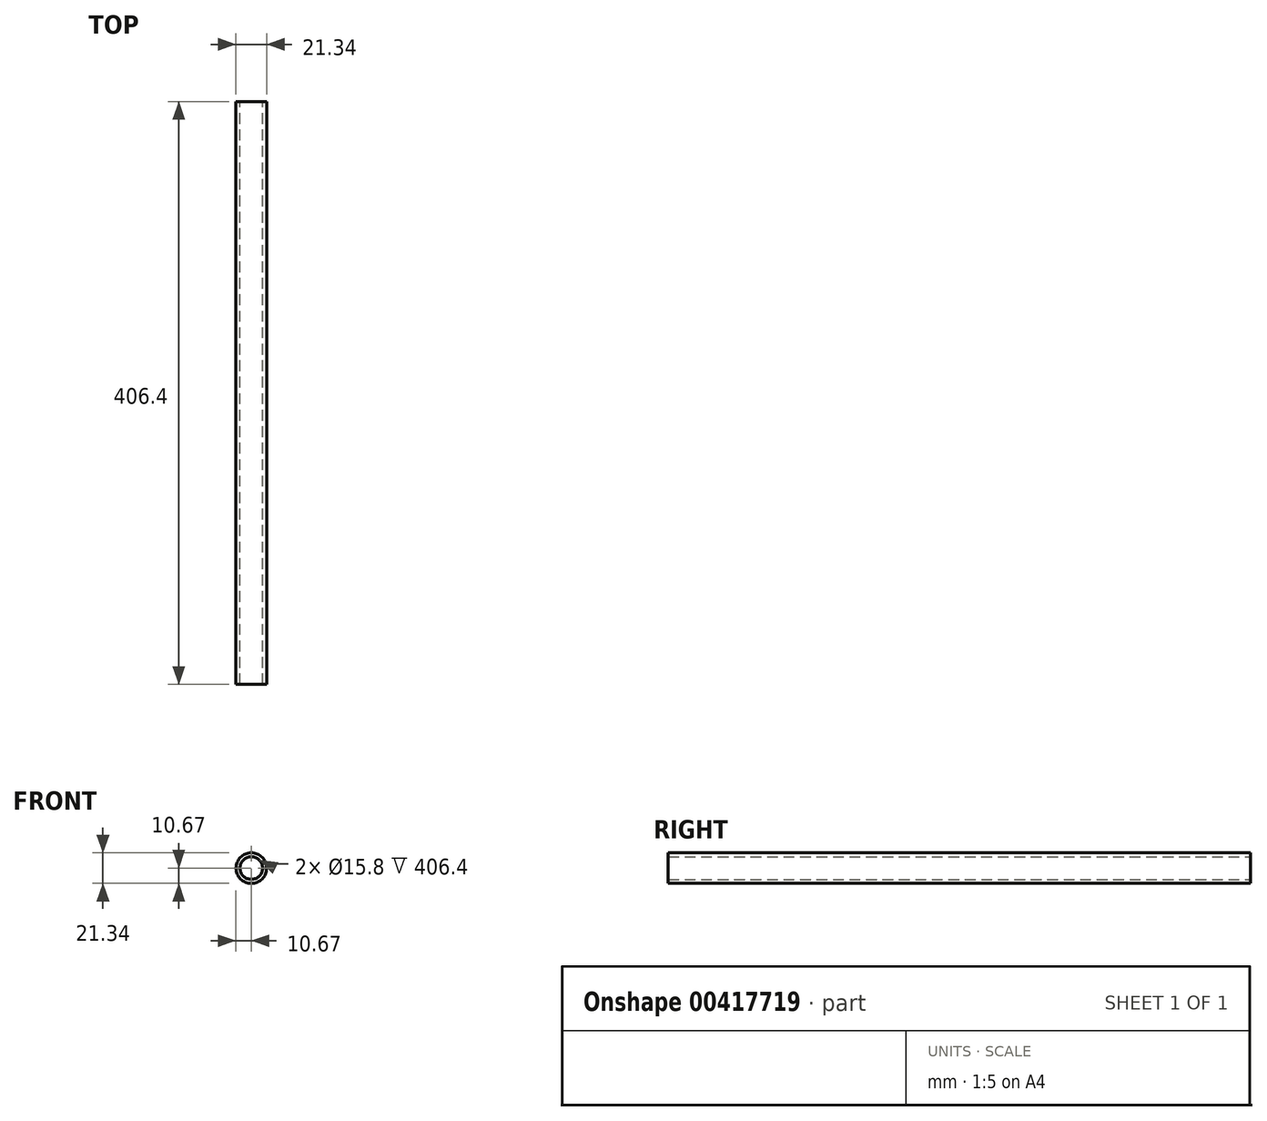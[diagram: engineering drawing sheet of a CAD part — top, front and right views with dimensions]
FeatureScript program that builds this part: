
annotation { "Feature Type Name" : "Feature", "Feature Type Description" : "" }
export const myFeature = defineFeature(function(context is Context, id is Id, definition is map)
    precondition{}
    {
        {
            var Q0;
            Q0=qCreatedBy(makeId("Front.planeOp"),FACE);
            var sketch = newSketch(context, id + "F0", { "sketchPlane" : qUnion([Q0])});
            skCircle(sketch, "E0", {"center": v(0, 0) * mm, "radius": 10.67 * mm});
            skCircle(sketch, "E1", {"center": v(0, 0) * mm, "radius": 7.9 * mm});
            skSolve(sketch);
        }
        {
            var Q0;
            Q0=makeQuery(id+"F0.imprint","IMPRINT",FACE,{"disambiguationData":[TD([[makeQuery(id+"F0.imprint","IMPRINT",EDGE,{"derivedFrom":sQuery(id+"F0.wireOp",EDGE,"E0")}),1.0]])]});
            extrude(context, id + "F1", {"entities" : qUnion([Q0]), "endBound" : BoundingType.SYMMETRIC, "depth" : 406.4 * mm});
        }
    });
